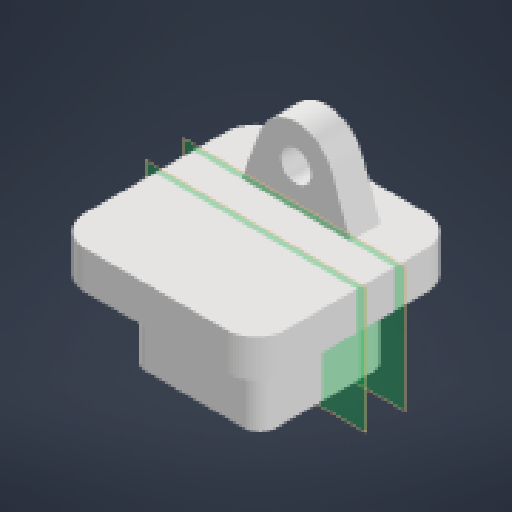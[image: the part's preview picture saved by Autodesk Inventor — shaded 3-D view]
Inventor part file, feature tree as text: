
AUTODESK INVENTOR PART (.ipt)
format: ipt  version: 2024 (Build 280153000, 153)  size: 224,256 bytes
history: native  units: mm
features: other x8, reference x8, extrude x3, sketch x3, fillet x2
ambient origin geometry x8: Origin, YZ Plane, XZ Plane, XY Plane, X Axis, Y Axis, Z Axis, Center Point
bodies: Body1 (feature_tree)
feature tree (24):
  other  "Твердое тело1"
  extrude  "Выдавливание1"  Depth=2.0mm
  extrude  "Выдавливание2"  Depth=10.0mm TaperAngle=0.0deg
  fillet  "Сопряжение1"  Radius=5.0mm
  fillet  "Сопряжение2"  Radius=2.0mm
  other  "РабПлоскость2"
  extrude  "Выдавливание3"  Depth=4.0mm
  sketch  "Эскиз1"
  reference  "Ссылка1"
  reference  "Ссылка2"
  reference  "Ссылка3"
  reference  "Ссылка4"
  sketch  "Эскиз2"
  reference  "Ссылка5"
  reference  "Ссылка6"
  reference  "Ссылка7"
  reference  "Ссылка8"
  other  "РабПлоскость1"
  sketch  "Эскиз3"
  parser-record x1  (decoder bookkeeping rows leaked as tree rows — omitted from the tree; the rows remain in map.json)
  other  "main_assembly.iam"
  other  "base_assembly:1"
  other  "shock_absorber_holder_down_200:1"
  other  "shock_absorber_holder_up:3"
note: 1 file-system path scrubbed to <path> (originals preserved in map.json)
